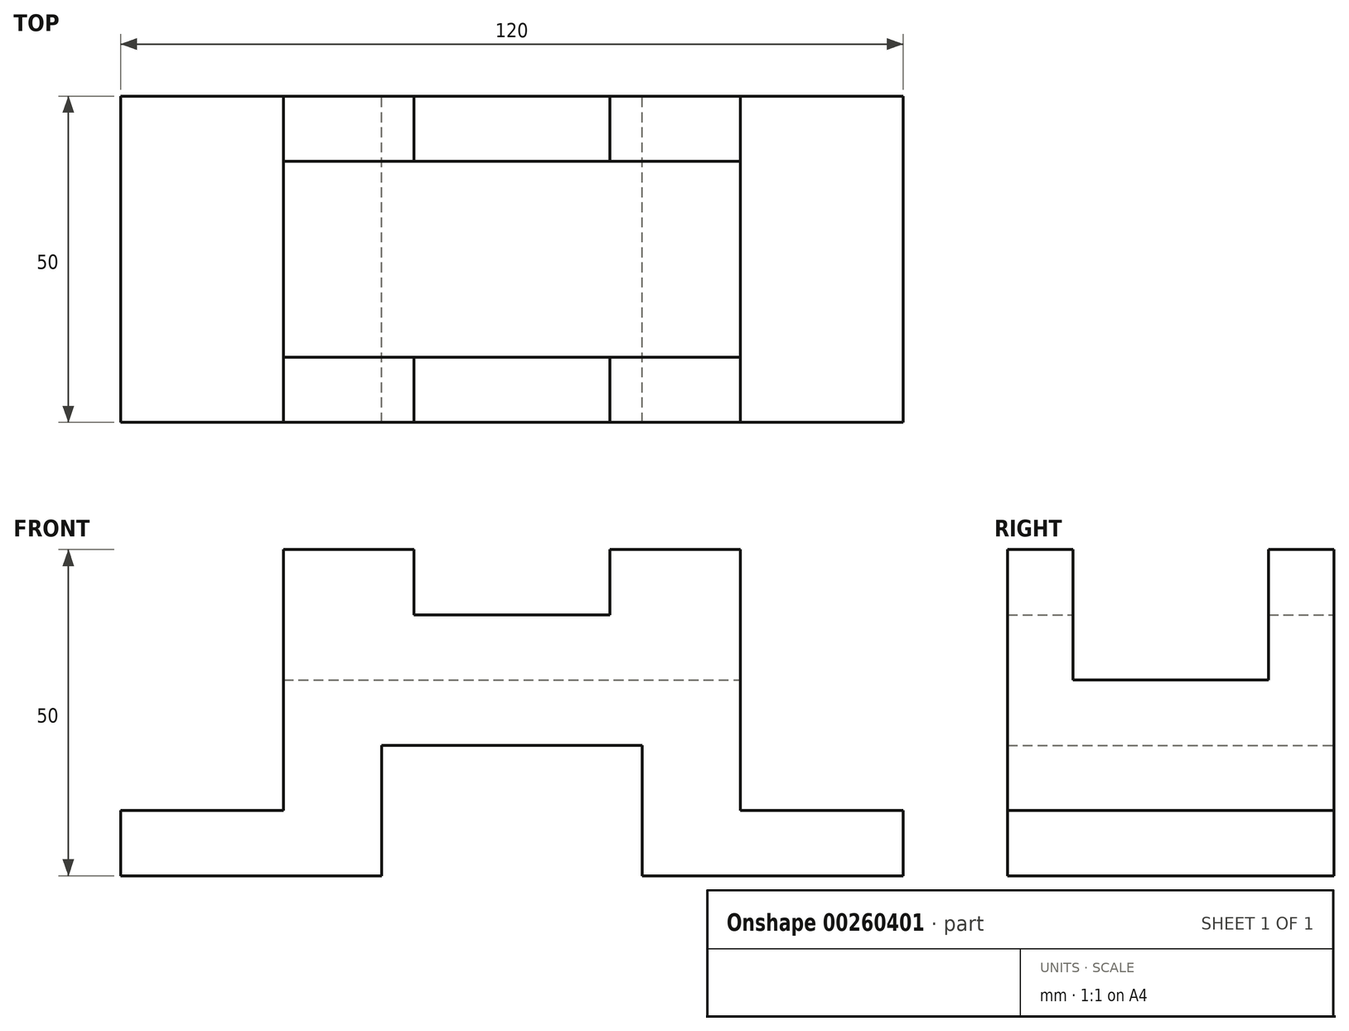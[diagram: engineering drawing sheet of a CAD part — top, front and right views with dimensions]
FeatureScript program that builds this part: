
annotation { "Feature Type Name" : "Feature", "Feature Type Description" : "" }
export const myFeature = defineFeature(function(context is Context, id is Id, definition is map)
    precondition{}
    {
        {
            assignVariable(context, id + "F0", {"name" : "A", "anyValue" : 50});
        }
        {
            var Q0;
            Q0=qCreatedBy(makeId("Front.planeOp"),FACE);
            var sketch = newSketch(context, id + "F1", { "sketchPlane" : qUnion([Q0])});
            skLineSegment(sketch, "E0", {"start": v(-20, 0) * mm, "end": v(-20, 20) * mm});
            skLineSegment(sketch, "E1", {"start": v(-20, 20) * mm, "end": v(20, 20) * mm});
            skLineSegment(sketch, "E2", {"start": v(20, 20) * mm, "end": v(20, 0) * mm});
            skLineSegment(sketch, "E3", {"start": v(20, 0) * mm, "end": v(60, 0) * mm});
            skLineSegment(sketch, "E4", {"start": v(60, 0) * mm, "end": v(60, 10) * mm});
            skLineSegment(sketch, "E5", {"start": v(60, 10) * mm, "end": v(35, 10) * mm});
            skLineSegment(sketch, "E6", {"start": v(35, 10) * mm, "end": v(35, 50) * mm});
            skLineSegment(sketch, "E7", {"start": v(35, 50) * mm, "end": v(15, 50) * mm});
            skLineSegment(sketch, "E8", {"start": v(15, 50) * mm, "end": v(15, 40) * mm});
            skLineSegment(sketch, "E9", {"start": v(15, 40) * mm, "end": v(-15, 40) * mm});
            skLineSegment(sketch, "E10", {"start": v(-15, 40) * mm, "end": v(-15, 50) * mm});
            skLineSegment(sketch, "E11", {"start": v(-15, 50) * mm, "end": v(-35, 50) * mm});
            skLineSegment(sketch, "E12", {"start": v(-35, 50) * mm, "end": v(-35, 10) * mm});
            skLineSegment(sketch, "E13", {"start": v(-35, 10) * mm, "end": v(-60, 10) * mm});
            skLineSegment(sketch, "E14", {"start": v(-60, 10) * mm, "end": v(-60, 0) * mm});
            skPoint(sketch, "E15", {"position": v(0, 20) * mm});
            skLineSegment(sketch, "E16", {"start": v(-60, 0) * mm, "end": v(-20, 0) * mm});
            skSolve(sketch);
        }
        {
            var Q0;
            Q0 = qSketchRegion(id + "F1", true);
            extrude(context, id + "F2", {"entities" : qUnion([Q0]), "depth" : (getVariable(context, 'A')) * mm});
        }
        {
            var Q0;
            Q0=makeQuery(id+"F2.opExtrude","SWEPT_FACE",FACE,{"disambiguationData":[OSD([sQuery(id+"F1.wireOp",EDGE,"E6")])]});
            var sketch = newSketch(context, id + "F3", { "sketchPlane" : qUnion([Q0])});
            skLineSegment(sketch, "E17.bottom", {"start": v(-40, 50) * mm, "end": v(-10, 50) * mm});
            skLineSegment(sketch, "E17.top", {"start": v(-40, 30) * mm, "end": v(-10, 30) * mm});
            skLineSegment(sketch, "E17.left", {"start": v(-40, 50) * mm, "end": v(-40, 30) * mm});
            skLineSegment(sketch, "E17.right", {"start": v(-10, 50) * mm, "end": v(-10, 30) * mm});
            skSolve(sketch);
        }
        {
            var Q0;
            Q0=makeQuery(id+"F3.imprint","IMPRINT",FACE,{"disambiguationData":[TD([[makeQuery(id+"F3.imprint","IMPRINT",EDGE,{"derivedFrom":sQuery(id+"F3.wireOp",EDGE,"E17.bottom")}),-1.0]])]});
            extrude(context, id + "F4", {"entities" : qUnion([Q0]), "operationType" : NewBodyOperationType.REMOVE, "oppositeDirection" : true, "depth" : 155 * mm});
        }
    });
